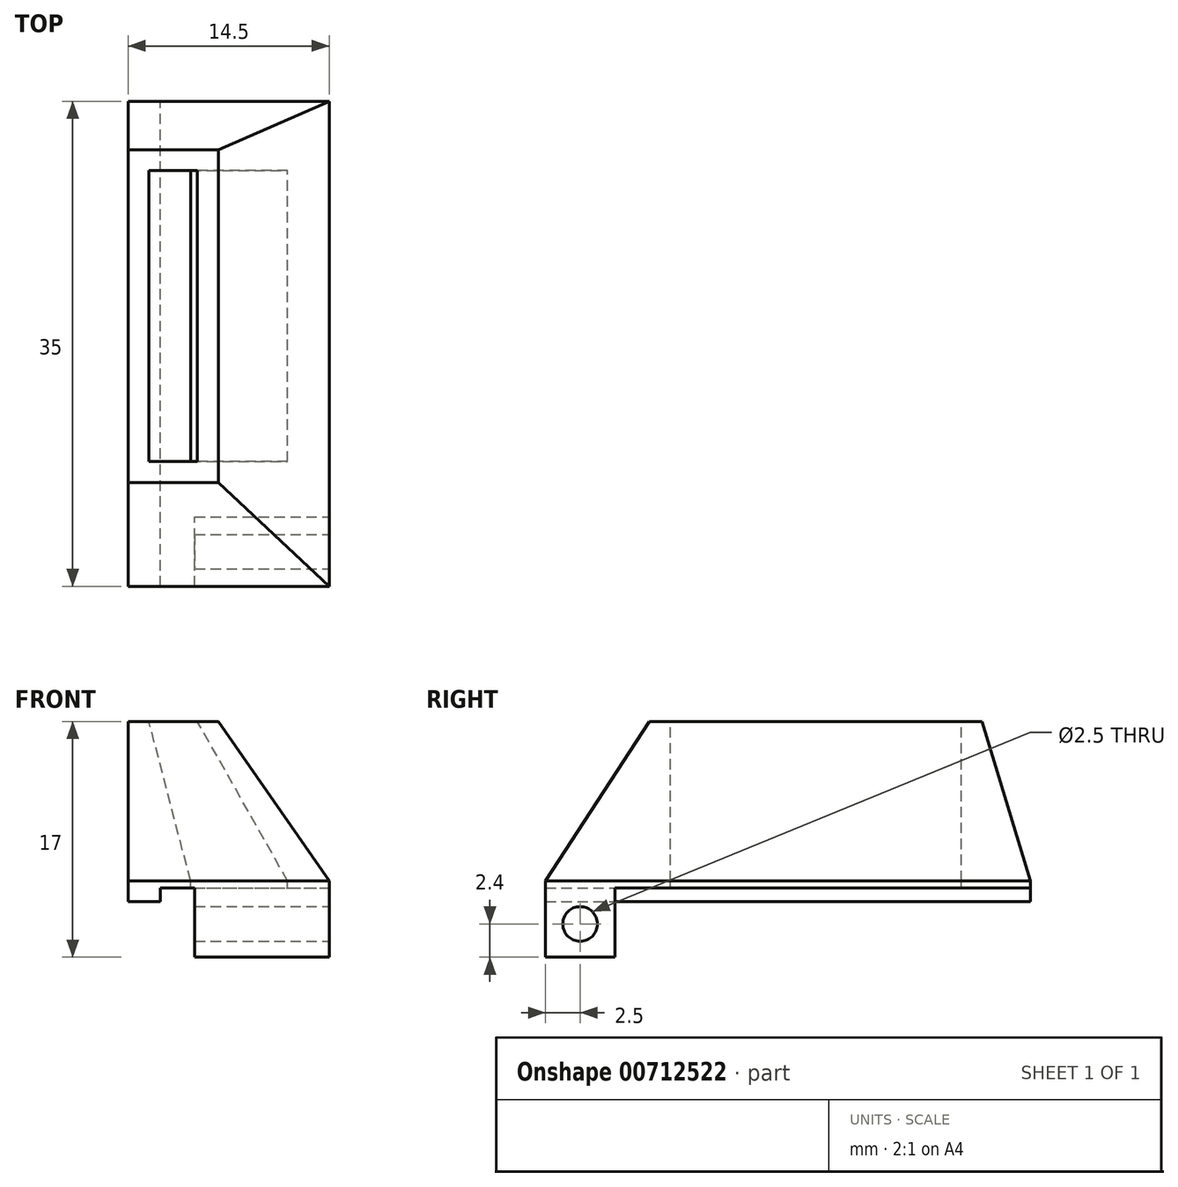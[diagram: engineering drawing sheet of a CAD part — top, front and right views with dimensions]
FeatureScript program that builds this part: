
annotation { "Feature Type Name" : "Feature", "Feature Type Description" : "" }
export const myFeature = defineFeature(function(context is Context, id is Id, definition is map)
    precondition{}
    {
        {
            var Q0;
            Q0=qCreatedBy(makeId("Top.planeOp"),FACE);
            var sketch = newSketch(context, id + "F0", { "sketchPlane" : qUnion([Q0])});
            skLineSegment(sketch, "E0.bottom", {"start": v(0, 0) * mm, "end": v(14.5, 0) * mm});
            skLineSegment(sketch, "E0.top", {"start": v(0, 35) * mm, "end": v(14.5, 35) * mm});
            skLineSegment(sketch, "E0.left", {"start": v(0, 0) * mm, "end": v(0, 35) * mm});
            skLineSegment(sketch, "E0.right", {"start": v(14.5, 0) * mm, "end": v(14.5, 35) * mm});
            skSolve(sketch);
        }
        {
            var Q0;
            Q0=qCreatedBy(makeId("Top.planeOp"),FACE);
            cPlane(context, id + "F1", {"entities" : qUnion([Q0]), "cplaneType" : CPlaneType.OFFSET, "offset" : 11.5 * mm, "width" : 150 * mm, "height" : 150 * mm});
        }
        {
            var Q0;
            Q0=qCreatedBy(id+"F1.planeOp",FACE);
            var sketch = newSketch(context, id + "F2", { "sketchPlane" : qUnion([Q0])});
            skLineSegment(sketch, "E1.bottom", {"start": v(0, 31.5) * mm, "end": v(6.5, 31.5) * mm});
            skLineSegment(sketch, "E1.top", {"start": v(0, 7.5) * mm, "end": v(6.5, 7.5) * mm});
            skLineSegment(sketch, "E1.left", {"start": v(0, 31.5) * mm, "end": v(0, 7.5) * mm});
            skLineSegment(sketch, "E1.right", {"start": v(6.5, 31.5) * mm, "end": v(6.5, 7.5) * mm});
            skSolve(sketch);
        }
        {
            var Q0;
            Q0=makeQuery(id+"F0.imprint","IMPRINT",FACE,{"disambiguationData":[TD([[makeQuery(id+"F0.imprint","IMPRINT",EDGE,{"derivedFrom":sQuery(id+"F0.wireOp",EDGE,"E0.bottom")}),1.0]])]});
            var Q1;
            Q1=makeQuery(id+"F2.imprint","IMPRINT",FACE,{"disambiguationData":[TD([[makeQuery(id+"F2.imprint","IMPRINT",EDGE,{"derivedFrom":sQuery(id+"F2.wireOp",EDGE,"E1.bottom")}),-1.0]])]});
            loft(context, id + "F3", {"sheetProfilesArray" : [{ "sheetProfileEntities" : qUnion([Q0]) }, { "sheetProfileEntities" : qUnion([Q1]) }]});
        }
        {
            var Q0;
            Q0=qCreatedBy(makeId("Top.planeOp"),FACE);
            var sketch = newSketch(context, id + "F4", { "sketchPlane" : qUnion([Q0])});
            skLineSegment(sketch, "E2.bottom", {"start": v(4.5, 9) * mm, "end": v(11.5, 9) * mm});
            skLineSegment(sketch, "E2.top", {"start": v(4.5, 30) * mm, "end": v(11.5, 30) * mm});
            skLineSegment(sketch, "E2.left", {"start": v(4.5, 9) * mm, "end": v(4.5, 30) * mm});
            skLineSegment(sketch, "E2.right", {"start": v(11.5, 9) * mm, "end": v(11.5, 30) * mm});
            skSolve(sketch);
        }
        {
            var Q0;
            Q0=qCreatedBy(id+"F1.planeOp",FACE);
            var sketch = newSketch(context, id + "F5", { "sketchPlane" : qUnion([Q0])});
            skLineSegment(sketch, "E3.bottom", {"start": v(1.5, 30) * mm, "end": v(5, 30) * mm});
            skLineSegment(sketch, "E3.top", {"start": v(1.5, 9) * mm, "end": v(5, 9) * mm});
            skLineSegment(sketch, "E3.left", {"start": v(1.5, 30) * mm, "end": v(1.5, 9) * mm});
            skLineSegment(sketch, "E3.right", {"start": v(5, 30) * mm, "end": v(5, 9) * mm});
            skSolve(sketch);
        }
        {
            var Q1;
            Q1=makeQuery(id+"F4.imprint","IMPRINT",FACE,{"disambiguationData":[TD([[makeQuery(id+"F4.imprint","IMPRINT",EDGE,{"derivedFrom":sQuery(id+"F4.wireOp",EDGE,"E2.bottom")}),1.0]])]});
            var Q2;
            Q2=makeQuery(id+"F5.imprint","IMPRINT",FACE,{"disambiguationData":[TD([[makeQuery(id+"F5.imprint","IMPRINT",EDGE,{"derivedFrom":sQuery(id+"F5.wireOp",EDGE,"E3.bottom")}),-1.0]])]});
            loft(context, id + "F6", {"operationType" : NewBodyOperationType.REMOVE, "sheetProfilesArray" : [{ "sheetProfileEntities" : qUnion([Q1]) }, { "sheetProfileEntities" : qUnion([Q2]) }]});
        }
        {
            var Q0;
            Q0=makeQuery(id+"F3.opLoft","CAP_FACE",FACE,{"disambiguationData":[OSD([makeQuery(id+"F0.imprint","IMPRINT",FACE,{"disambiguationData":[TD([[makeQuery(id+"F0.imprint","IMPRINT",EDGE,{"derivedFrom":sQuery(id+"F0.wireOp",EDGE,"E0.bottom")}),1.0]])]})])],"isStart":true});
            extrude(context, id + "F7", {"entities" : qUnion([Q0]), "operationType" : NewBodyOperationType.ADD, "depth" : 0.5 * mm, "offsetDistance" : 25 * mm});
        }
        {
            var Q0;
            Q0=makeQuery(id+"F7.opExtrude","CAP_FACE",FACE,{"disambiguationData":[OSD([makeQuery(id+"F0.imprint","IMPRINT",FACE,{"disambiguationData":[TD([[makeQuery(id+"F0.imprint","IMPRINT",EDGE,{"derivedFrom":sQuery(id+"F0.wireOp",EDGE,"E0.bottom")}),1.0]])]})])],"isStart":false});
            var sketch = newSketch(context, id + "F8", { "sketchPlane" : qUnion([Q0])});
            skLineSegment(sketch, "E4.bottom", {"start": v(0, 0) * mm, "end": v(2.3, 0) * mm});
            skLineSegment(sketch, "E4.top", {"start": v(0, -35) * mm, "end": v(2.3, -35) * mm});
            skLineSegment(sketch, "E4.left", {"start": v(0, 0) * mm, "end": v(0, -35) * mm});
            skLineSegment(sketch, "E4.right", {"start": v(2.3, 0) * mm, "end": v(2.3, -35) * mm});
            skSolve(sketch);
        }
        {
            var Q0;
            Q0=makeQuery(id+"F8.imprint","IMPRINT",FACE,{"disambiguationData":[TD([[makeQuery(id+"F8.imprint","IMPRINT",EDGE,{"derivedFrom":sQuery(id+"F8.wireOp",EDGE,"E4.bottom")}),-1.0]])]});
            extrude(context, id + "F9", {"entities" : qUnion([Q0]), "operationType" : NewBodyOperationType.ADD, "depth" : 1 * mm, "offsetDistance" : 25 * mm});
        }
        {
            var Q0;
            Q0=makeQuery(id+"F7.opExtrude","CAP_FACE",FACE,{"disambiguationData":[OSD([makeQuery(id+"F0.imprint","IMPRINT",FACE,{"disambiguationData":[TD([[makeQuery(id+"F0.imprint","IMPRINT",EDGE,{"derivedFrom":sQuery(id+"F0.wireOp",EDGE,"E0.bottom")}),1.0]])]})])],"isStart":false});
            var sketch = newSketch(context, id + "F10", { "sketchPlane" : qUnion([Q0])});
            skLineSegment(sketch, "E5.bottom", {"start": v(4.8, 0) * mm, "end": v(14.5, 0) * mm});
            skLineSegment(sketch, "E5.top", {"start": v(4.8, -5) * mm, "end": v(14.5, -5) * mm});
            skLineSegment(sketch, "E5.left", {"start": v(4.8, 0) * mm, "end": v(4.8, -5) * mm});
            skLineSegment(sketch, "E5.right", {"start": v(14.5, 0) * mm, "end": v(14.5, -5) * mm});
            skLineSegment(sketch, "E6.bottom", {"start": v(14.5, -5) * mm, "end": v(12.7, -5) * mm});
            skLineSegment(sketch, "E6.top", {"start": v(14.5, -35) * mm, "end": v(12.7, -35) * mm});
            skLineSegment(sketch, "E6.left", {"start": v(14.5, -5) * mm, "end": v(14.5, -35) * mm});
            skLineSegment(sketch, "E6.right", {"start": v(12.7, -5) * mm, "end": v(12.7, -35) * mm});
            skSolve(sketch);
        }
        {
            var Q0;
            Q0=makeQuery(id+"F10.imprint","IMPRINT",FACE,{"disambiguationData":[TD([[makeQuery(id+"F10.imprint","IMPRINT",EDGE,{"derivedFrom":sQuery(id+"F10.wireOp",EDGE,"E5.bottom")}),-1.0]])]});
            var Q1;
            Q1=makeQuery(id+"F10.imprint","IMPRINT",FACE,{"disambiguationData":[TD([[makeQuery(id+"F10.imprint","IMPRINT",EDGE,{"derivedFrom":sQuery(id+"F10.wireOp",EDGE,"E6.bottom")}),1.0]])]});
            extrude(context, id + "F11", {"entities" : qUnion([Q0, Q1]), "operationType" : NewBodyOperationType.ADD, "depth" : 5 * mm, "offsetDistance" : 25 * mm});
        }
        {
            var Q0;
            Q0=makeQuery(id+"F11.boolean.opBoolean","MERGE",FACE,{"derivedFrom":[makeQuery(id+"F7.opExtrude","SWEPT_FACE",FACE,{"disambiguationData":[OSD([sQuery(id+"F0.wireOp",EDGE,"E0.bottom"),sQuery(id+"F0.wireOp",EDGE,"E0.top"),sQuery(id+"F0.wireOp",EDGE,"E0.right")])]}),makeQuery(id+"F11.opExtrude","SWEPT_FACE",FACE,{"disambiguationData":[OSD([sQuery(id+"F10.wireOp",EDGE,"E5.right"),sQuery(id+"F10.wireOp",EDGE,"E6.left")])]})]});
            var sketch = newSketch(context, id + "F12", { "sketchPlane" : qUnion([Q0])});
            skCircle(sketch, "E7", {"center": v(2.5, -3.1) * mm, "radius": 1.25 * mm});
            skCircle(sketch, "E8", {"center": v(32.4, -3.1) * mm, "radius": 1.25 * mm});
            skSolve(sketch);
        }
        {
            var Q0;
            Q0=makeQuery(id+"F12.imprint","IMPRINT",FACE,{"disambiguationData":[TD([[makeQuery(id+"F12.imprint","IMPRINT",EDGE,{"derivedFrom":sQuery(id+"F12.wireOp",EDGE,"E7")}),1.0]])]});
            var Q1;
            Q1=makeQuery(id+"F12.imprint","IMPRINT",FACE,{"disambiguationData":[TD([[makeQuery(id+"F12.imprint","IMPRINT",EDGE,{"derivedFrom":sQuery(id+"F12.wireOp",EDGE,"E8")}),1.0]])]});
            extrude(context, id + "F13", {"entities" : qUnion([Q0, Q1]), "operationType" : NewBodyOperationType.REMOVE, "endBound" : BoundingType.THROUGH_ALL, "oppositeDirection" : true, "depth" : 25 * mm, "offsetDistance" : 25 * mm});
        }
    });
